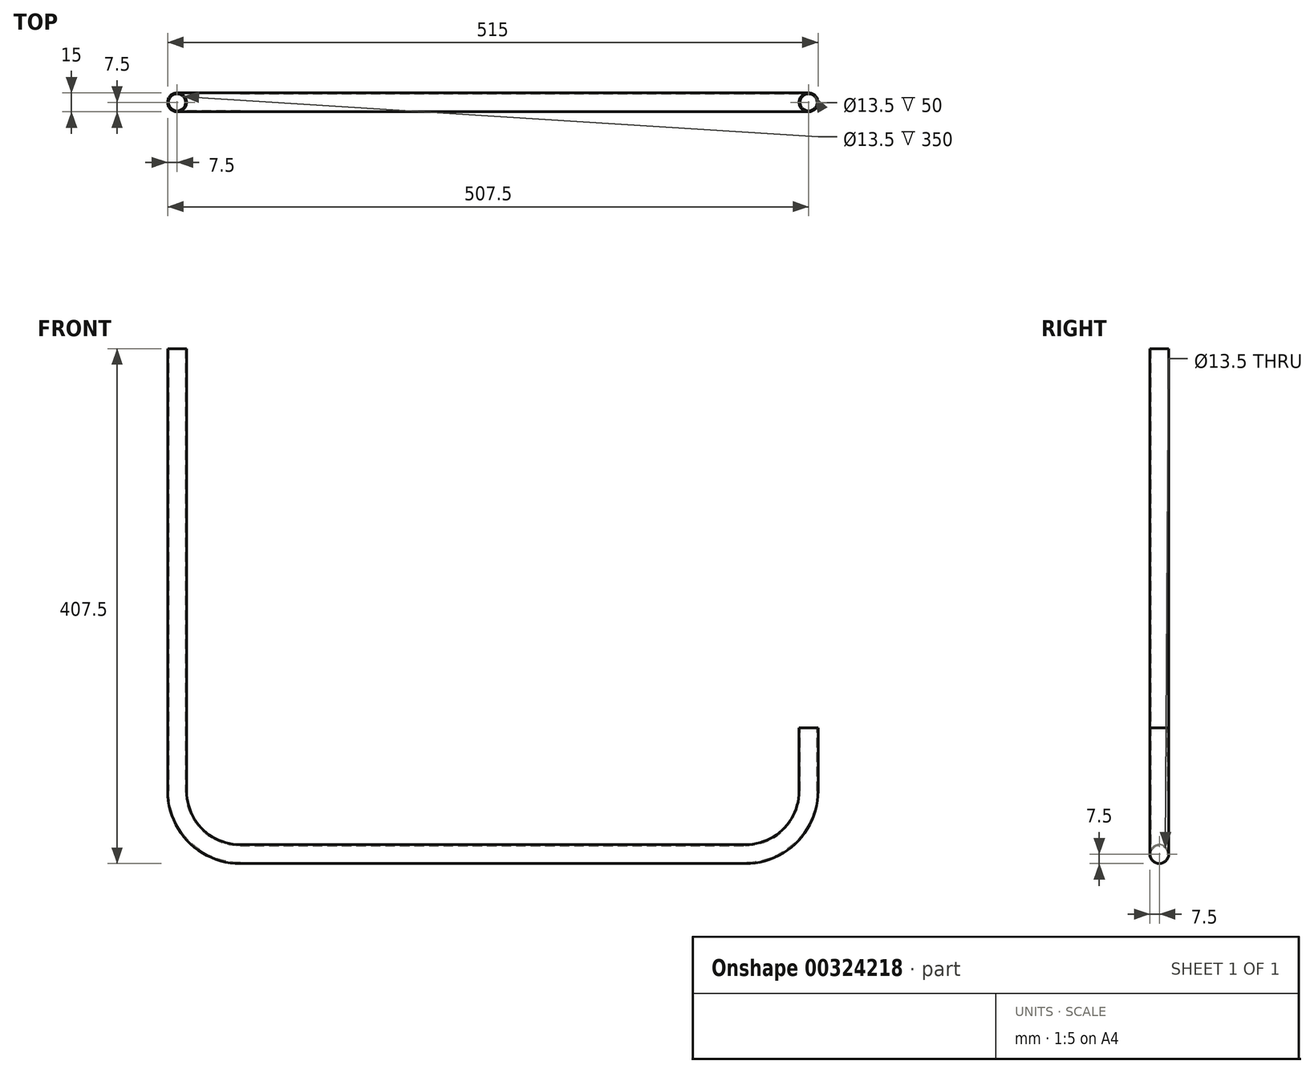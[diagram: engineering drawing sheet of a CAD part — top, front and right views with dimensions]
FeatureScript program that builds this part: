
annotation { "Feature Type Name" : "Feature", "Feature Type Description" : "" }
export const myFeature = defineFeature(function(context is Context, id is Id, definition is map)
    precondition{}
    {
        {
            var Q0;
            Q0=qCreatedBy(makeId("Front.planeOp"),FACE);
            var sketch = newSketch(context, id + "F0", { "sketchPlane" : qUnion([Q0])});
            skLineSegment(sketch, "E0", {"start": v(0, 0) * mm, "end": v(0, -350) * mm});
            skLineSegment(sketch, "E1", {"start": v(50, -400) * mm, "end": v(450, -400) * mm});
            skLineSegment(sketch, "E2", {"start": v(500, -350) * mm, "end": v(500, -300) * mm});
            skPoint(sketch, "E3.visualSharp", {"position": v(0, -400) * mm});
            skArc(sketch, "E3.filletArc", {"start": v(0, -350) * mm, "mid": v(14.64, -385.36) * mm, "end": v(50, -400) * mm});
            skPoint(sketch, "E4.visualSharp", {"position": v(500, -400) * mm});
            skArc(sketch, "E4.filletArc", {"start": v(450, -400) * mm, "mid": v(485.36, -385.36) * mm, "end": v(500, -350) * mm});
            skSolve(sketch);
        }
        {
            var Q0;
            Q0=qCreatedBy(makeId("Top.planeOp"),FACE);
            var sketch = newSketch(context, id + "F1", { "sketchPlane" : qUnion([Q0])});
            skCircle(sketch, "E5", {"center": v(0, 0) * mm, "radius": 7.5 * mm});
            skCircle(sketch, "E6", {"center": v(0, 0) * mm, "radius": 6.75 * mm});
            skSolve(sketch);
        }
        {
            var Q0;
            Q0=makeQuery(id+"F1.imprint","IMPRINT",FACE,{"disambiguationData":[TD([[makeQuery(id+"F1.imprint","IMPRINT",EDGE,{"derivedFrom":sQuery(id+"F1.wireOp",EDGE,"E5")}),1.0]])]});
            var Q1;
            Q1=sQuery(id+"F0.wireOp",EDGE,"E0");
            var Q2;
            Q2=sQuery(id+"F0.wireOp",EDGE,"E3.filletArc");
            var Q3;
            Q3=sQuery(id+"F0.wireOp",EDGE,"E1");
            var Q4;
            Q4=sQuery(id+"F0.wireOp",EDGE,"E4.filletArc");
            var Q5;
            Q5=sQuery(id+"F0.wireOp",EDGE,"E2");
            sweep(context, id + "F2", {"profiles" : qUnion([Q0]), "path" : qUnion([Q1, Q2, Q3, Q4, Q5])});
        }
    });
